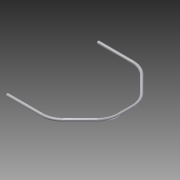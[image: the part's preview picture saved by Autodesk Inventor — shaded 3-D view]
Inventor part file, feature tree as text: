
AUTODESK INVENTOR PART (.ipt)
format: ipt  version: 2014 SP1 (Build 180222100, 222)  size: 119,808 bytes
history: native  units: in
note: dims shown in document units (in); Inventor stores cm internally (conversion verified against a paired STEP export)
features: sweep x1, mirror x1, sketch x1
ambient origin geometry x8: Origin, YZ Plane, XZ Plane, XY Plane, X Axis, Y Axis, Z Axis, Center Point
bodies: Solid1 (feature_tree)
feature tree (3):
  sweep  "Sweep1"
  mirror  "Mirror1"
  sketch  "Sketch1"  dims[d0=0.5in d1=0.035in d2=1.25in d3=7.0in d4=13.25in d5=0.0in d6=8.25in d7=45.0deg d8=45.0deg d9=4.0in d10=4.0in]
